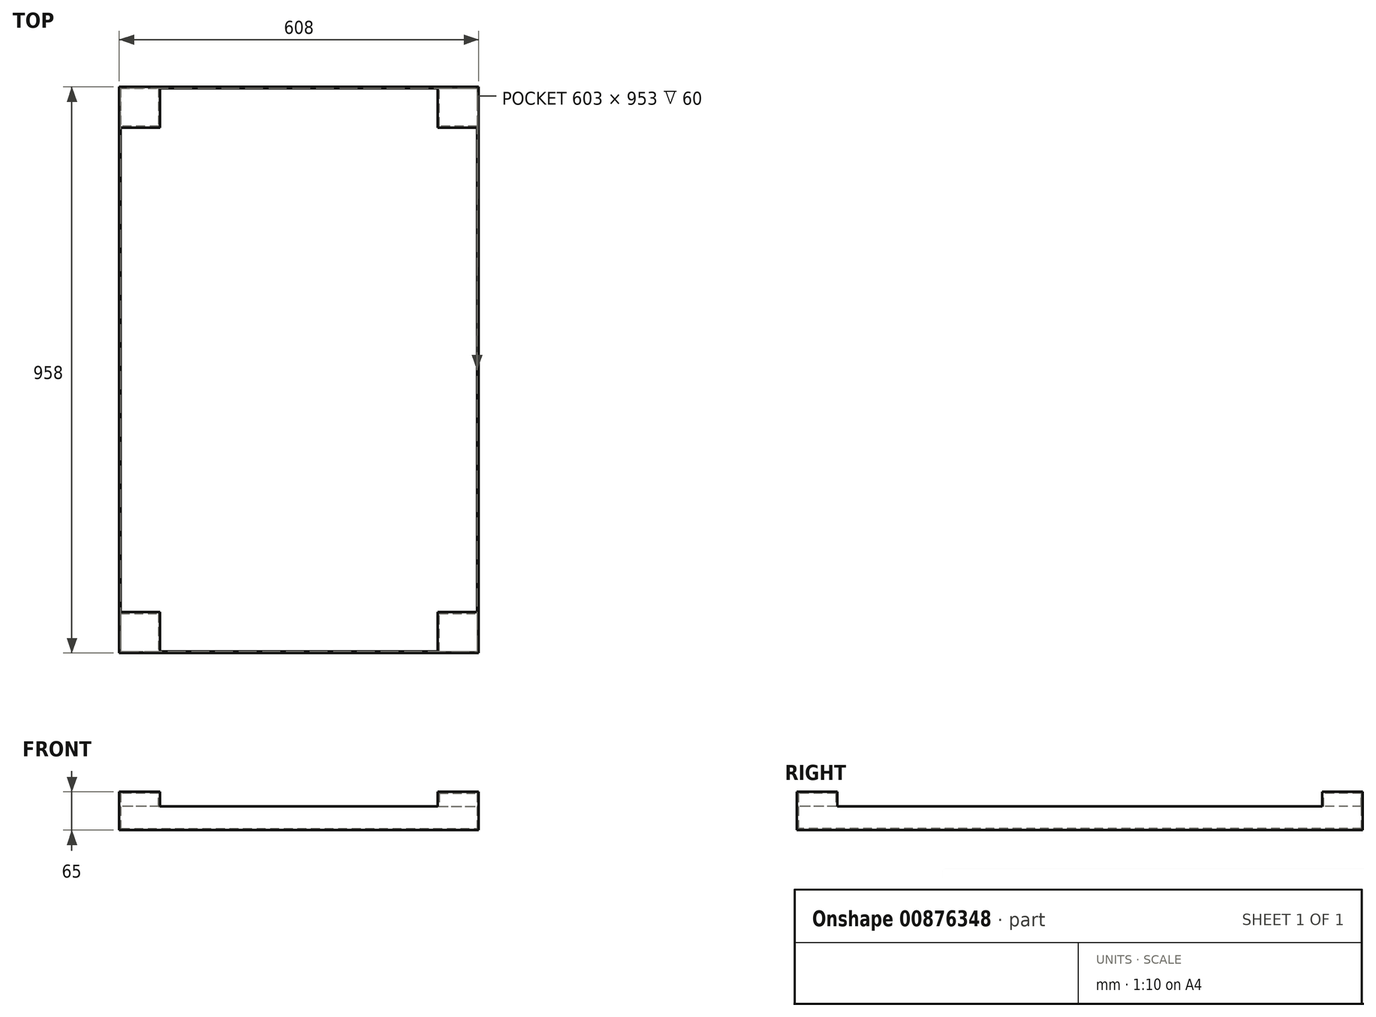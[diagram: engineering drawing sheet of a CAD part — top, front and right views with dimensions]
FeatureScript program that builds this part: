
annotation { "Feature Type Name" : "Feature", "Feature Type Description" : "" }
export const myFeature = defineFeature(function(context is Context, id is Id, definition is map)
    precondition{}
    {
        {
            var Q0;
            Q0=qCreatedBy(makeId("Top.planeOp"),FACE);
            var sketch = newSketch(context, id + "F0", { "sketchPlane" : qUnion([Q0])});
            skLineSegment(sketch, "E0.bottom", {"start": v(-304, 479) * mm, "end": v(304, 479) * mm});
            skLineSegment(sketch, "E0.top", {"start": v(-304, -479) * mm, "end": v(304, -479) * mm});
            skLineSegment(sketch, "E0.left", {"start": v(-304, 479) * mm, "end": v(-304, -479) * mm});
            skLineSegment(sketch, "E0.right", {"start": v(304, 479) * mm, "end": v(304, -479) * mm});
            skSolve(sketch);
        }
        {
            var Q0;
            Q0=makeQuery(id+"F0.imprint","IMPRINT",FACE,{"disambiguationData":[TD([[makeQuery(id+"F0.imprint","IMPRINT",EDGE,{"derivedFrom":sQuery(id+"F0.wireOp",EDGE,"E0.bottom")}),-1.0]])]});
            extrude(context, id + "F1", {"entities" : qUnion([Q0]), "depth" : 65 * mm, "offsetDistance" : 25 * mm});
        }
        {
            var Q0;
            Q0=makeQuery(id+"F1.opExtrude","CAP_FACE",FACE,{"disambiguationData":[OSD([sQuery(id+"F0.wireOp",EDGE,"E0.bottom"),sQuery(id+"F0.wireOp",EDGE,"E0.top"),sQuery(id+"F0.wireOp",EDGE,"E0.left"),sQuery(id+"F0.wireOp",EDGE,"E0.right")])],"isStart":false});
            var sketch = newSketch(context, id + "F2", { "sketchPlane" : qUnion([Q0])});
            skLineSegment(sketch, "E1", {"start": v(-235, 533.03) * mm, "end": v(-235, 410) * mm});
            skLineSegment(sketch, "E2", {"start": v(-235, 410) * mm, "end": v(-362.35, 410) * mm});
            skLineSegment(sketch, "E3", {"start": v(-362.35, 410) * mm, "end": v(-362.35, -410) * mm});
            skLineSegment(sketch, "E4", {"start": v(-362.35, -410) * mm, "end": v(-235, -410) * mm});
            skLineSegment(sketch, "E5", {"start": v(-235, -410) * mm, "end": v(-235, -557.46) * mm});
            skLineSegment(sketch, "E6", {"start": v(-235, -557.46) * mm, "end": v(235, -557.46) * mm});
            skLineSegment(sketch, "E7", {"start": v(235, -557.46) * mm, "end": v(235, -410) * mm});
            skLineSegment(sketch, "E8", {"start": v(235, -410) * mm, "end": v(358.74, -410) * mm});
            skLineSegment(sketch, "E9", {"start": v(358.74, -410) * mm, "end": v(358.74, 410) * mm});
            skLineSegment(sketch, "E10", {"start": v(358.74, 410) * mm, "end": v(235, 410) * mm});
            skLineSegment(sketch, "E11", {"start": v(235, 410) * mm, "end": v(235, 533.03) * mm});
            skLineSegment(sketch, "E12", {"start": v(235, 533.03) * mm, "end": v(-235, 533.03) * mm});
            skSolve(sketch);
        }
        {
            var Q0;
            Q0 = qSketchRegion(id + "F2", true);
            extrude(context, id + "F3", {"entities" : qUnion([Q0]), "operationType" : NewBodyOperationType.REMOVE, "oppositeDirection" : true, "depth" : 25 * mm, "offsetDistance" : 25 * mm});
        }
        {
            var Q0;
            Q0=makeQuery(id+"F3.boolean.opBoolean","COPY",FACE,{"derivedFrom":makeQuery(id+"F3.opExtrude","CAP_FACE",FACE,{"disambiguationData":[OSD([sQuery(id+"F2.wireOp",EDGE,"E1"),sQuery(id+"F2.wireOp",EDGE,"E2"),sQuery(id+"F2.wireOp",EDGE,"E3"),sQuery(id+"F2.wireOp",EDGE,"E4"),sQuery(id+"F2.wireOp",EDGE,"E5"),sQuery(id+"F2.wireOp",EDGE,"E6"),sQuery(id+"F2.wireOp",EDGE,"E7"),sQuery(id+"F2.wireOp",EDGE,"E8"),sQuery(id+"F2.wireOp",EDGE,"E9"),sQuery(id+"F2.wireOp",EDGE,"E10"),sQuery(id+"F2.wireOp",EDGE,"E11"),sQuery(id+"F2.wireOp",EDGE,"E12")])],"isStart":false})});
            shell(context, id + "F4", {"entities" : qUnion([Q0]), "thickness" : 2.5 * mm});
        }
    });
